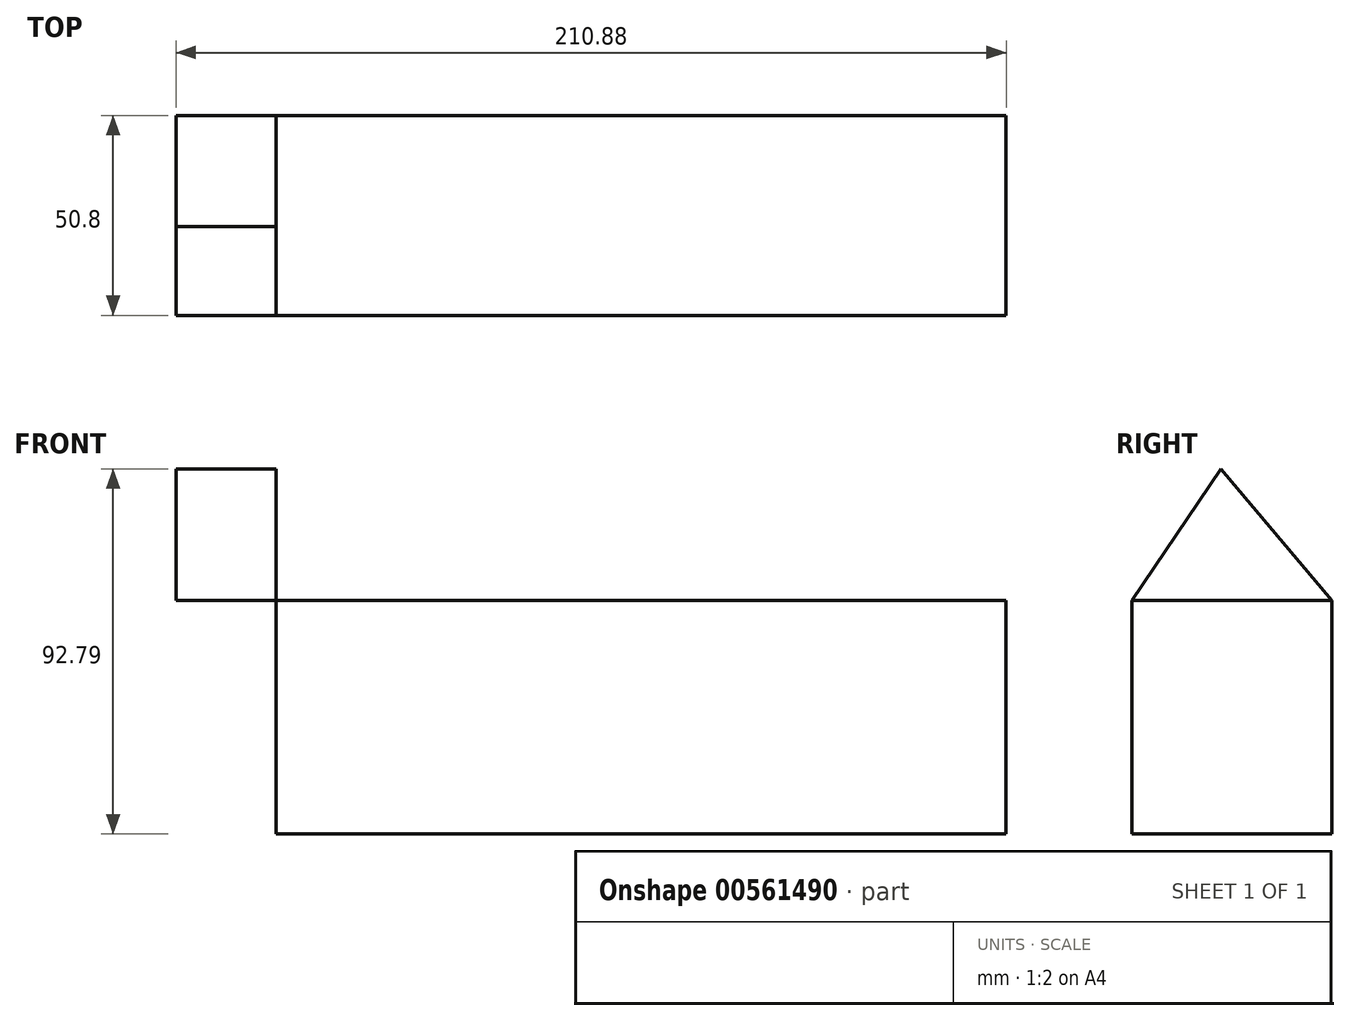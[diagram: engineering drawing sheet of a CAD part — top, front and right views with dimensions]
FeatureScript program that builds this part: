
annotation { "Feature Type Name" : "Feature", "Feature Type Description" : "" }
export const myFeature = defineFeature(function(context is Context, id is Id, definition is map)
    precondition{}
    {
        {
            var Q0;
            Q0=qCreatedBy(makeId("Front.planeOp"),FACE);
            var sketch = newSketch(context, id + "F0", { "sketchPlane" : qUnion([Q0])});
            skLineSegment(sketch, "E0.bottom", {"start": v(-113.54, 31.2) * mm, "end": v(71.94, 31.2) * mm});
            skLineSegment(sketch, "E0.top", {"start": v(-113.54, -28.17) * mm, "end": v(71.94, -28.17) * mm});
            skLineSegment(sketch, "E0.left", {"start": v(-113.54, 31.2) * mm, "end": v(-113.54, -28.17) * mm});
            skLineSegment(sketch, "E0.right", {"start": v(71.94, 31.2) * mm, "end": v(71.94, -28.17) * mm});
            skSolve(sketch);
        }
        {
            var Q0;
            Q0=makeQuery(id+"F0.imprint","IMPRINT",FACE,{"disambiguationData":[TD([[makeQuery(id+"F0.imprint","IMPRINT",EDGE,{"derivedFrom":sQuery(id+"F0.wireOp",EDGE,"E0.bottom")}),-1.0]])]});
            extrude(context, id + "F1", {"entities" : qUnion([Q0]), "depth" : 50.8 * mm, "offsetDistance" : 25.4 * mm});
        }
        {
            var Q0;
            Q0=makeQuery(id+"F1.opExtrude","SWEPT_FACE",FACE,{"disambiguationData":[OSD([sQuery(id+"F0.wireOp",EDGE,"E0.left")])]});
            var sketch = newSketch(context, id + "F2", { "sketchPlane" : qUnion([Q0])});
            skLineSegment(sketch, "E1", {"start": v(0, 31.2) * mm, "end": v(28.26, 64.62) * mm});
            skLineSegment(sketch, "E2", {"start": v(28.26, 64.62) * mm, "end": v(50.8, 31.2) * mm});
            skLineSegment(sketch, "E3", {"start": v(50.8, 31.2) * mm, "end": v(0, 31.2) * mm});
            skSolve(sketch);
        }
        {
            var Q0;
            Q0=makeQuery(id+"F2.imprint","IMPRINT",FACE,{"disambiguationData":[TD([[makeQuery(id+"F2.imprint","IMPRINT",EDGE,{"derivedFrom":sQuery(id+"F2.wireOp",EDGE,"E1")}),-1.0]])]});
            extrude(context, id + "F3", {"entities" : qUnion([Q0]), "depth" : 25.4 * mm, "offsetDistance" : 25.4 * mm});
        }
    });
